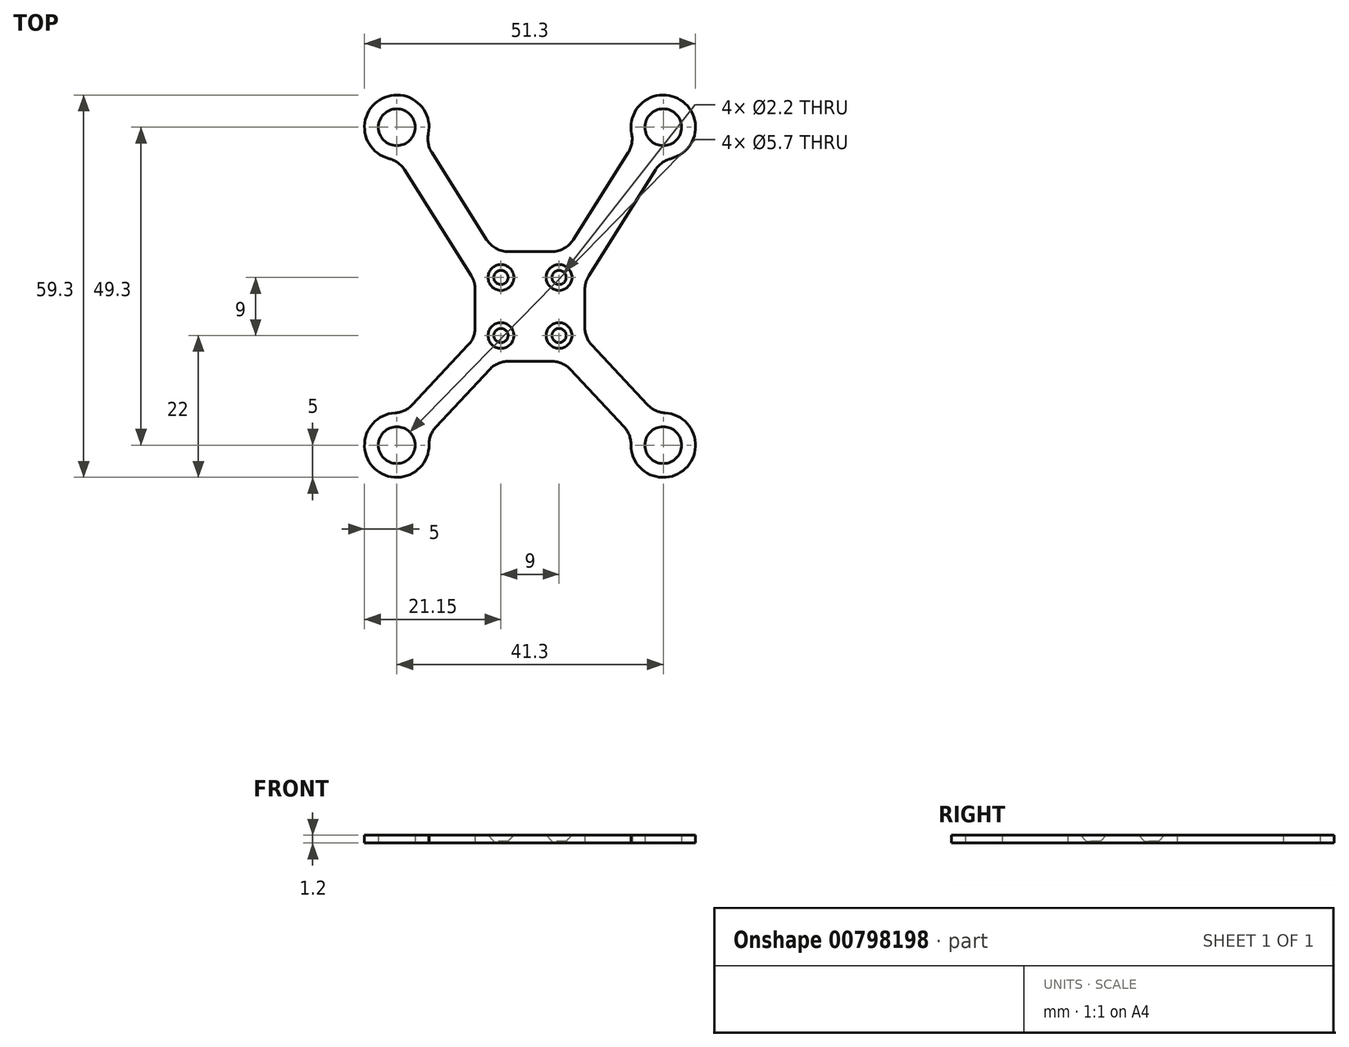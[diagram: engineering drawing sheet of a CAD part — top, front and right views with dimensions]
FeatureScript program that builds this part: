
annotation { "Feature Type Name" : "Feature", "Feature Type Description" : "" }
export const myFeature = defineFeature(function(context is Context, id is Id, definition is map)
    precondition{}
    {
        {
            var Q0;
            Q0=qCreatedBy(makeId("Top.planeOp"),FACE);
            var sketch = newSketch(context, id + "F0", { "sketchPlane" : qUnion([Q0])});
            skLineSegment(sketch, "E0.bottom", {"start": v(14.65, 24.65) * mm, "end": v(-14.65, 24.65) * mm});
            skLineSegment(sketch, "E0.top", {"start": v(14.65, -24.65) * mm, "end": v(-14.65, -24.65) * mm});
            skLineSegment(sketch, "E0.left", {"start": v(14.65, 24.65) * mm, "end": v(14.65, -24.65) * mm});
            skLineSegment(sketch, "E0.right", {"start": v(-14.65, 24.65) * mm, "end": v(-14.65, -24.65) * mm});
            skPoint(sketch, "E0.middle", {"position": v(0, 0) * mm});
            skLineSegment(sketch, "E1.bottom", {"start": v(4.5, 1.35) * mm, "end": v(-4.5, 1.35) * mm});
            skLineSegment(sketch, "E1.top", {"start": v(4.5, -7.65) * mm, "end": v(-4.5, -7.65) * mm});
            skLineSegment(sketch, "E1.left", {"start": v(4.5, 1.35) * mm, "end": v(4.5, -7.65) * mm});
            skLineSegment(sketch, "E1.right", {"start": v(-4.5, 1.35) * mm, "end": v(-4.5, -7.65) * mm});
            skPoint(sketch, "E1.middle", {"position": v(0, -3.15) * mm});
            skSolve(sketch);
        }
        {
            var Q0;
            Q0=qCreatedBy(makeId("Top.planeOp"),FACE);
            var sketch = newSketch(context, id + "F1", { "sketchPlane" : qUnion([Q0])});
            skLineSegment(sketch, "E2.bottom", {"start": v(8.5, 5.35) * mm, "end": v(-8.5, 5.35) * mm, "construction": true});
            skLineSegment(sketch, "E2.top", {"start": v(8.5, -11.65) * mm, "end": v(-8.5, -11.65) * mm, "construction": true});
            skLineSegment(sketch, "E2.left", {"start": v(8.5, 5.35) * mm, "end": v(8.5, -11.65) * mm, "construction": true});
            skLineSegment(sketch, "E2.right", {"start": v(-8.5, 5.35) * mm, "end": v(-8.5, -11.65) * mm, "construction": true});
            skPoint(sketch, "E2.middle", {"position": v(0, -3.15) * mm});
            skCircle(sketch, "E3", {"center": v(-4.5, 1.35) * mm, "radius": 1.1 * mm});
            skCircle(sketch, "E4", {"center": v(4.5, 1.35) * mm, "radius": 1.1 * mm});
            skCircle(sketch, "E5", {"center": v(4.5, -7.65) * mm, "radius": 1.1 * mm});
            skCircle(sketch, "E6", {"center": v(-4.5, -7.65) * mm, "radius": 1.1 * mm});
            skCircle(sketch, "E7", {"center": v(-20.65, -24.65) * mm, "radius": 2.85 * mm});
            skCircle(sketch, "E8", {"center": v(-20.65, -24.65) * mm, "radius": 5 * mm, "construction": true});
            skCircle(sketch, "E9.MirrorC", {"center": v(20.65, -24.65) * mm, "radius": 2.85 * mm});
            skCircle(sketch, "E10.MirrorC", {"center": v(20.65, -24.65) * mm, "radius": 5 * mm, "construction": true});
            skCircle(sketch, "E11.MirrorC", {"center": v(20.65, 24.65) * mm, "radius": 2.85 * mm});
            skCircle(sketch, "E12.MirrorC", {"center": v(20.65, 24.65) * mm, "radius": 5 * mm, "construction": true});
            skCircle(sketch, "E13.MirrorC", {"center": v(-20.65, 24.65) * mm, "radius": 2.85 * mm});
            skCircle(sketch, "E14.MirrorC", {"center": v(-20.65, 24.65) * mm, "radius": 5 * mm, "construction": true});
            skLineSegment(sketch, "E15", {"start": v(-20.65, 24.65) * mm, "end": v(-8.5, 5.35) * mm, "construction": true});
            skLineSegment(sketch, "E16", {"start": v(8.5, 5.35) * mm, "end": v(20.65, 24.65) * mm, "construction": true});
            skLineSegment(sketch, "E17", {"start": v(8.5, -11.65) * mm, "end": v(20.65, -24.65) * mm, "construction": true});
            skLineSegment(sketch, "E18", {"start": v(-8.5, -11.65) * mm, "end": v(-20.65, -24.65) * mm, "construction": true});
            skLineSegment(sketch, "E19", {"start": v(-19.52, -19.78) * mm, "end": v(-8.5, -7.99) * mm});
            skLineSegment(sketch, "E20", {"start": v(-15.87, -23.2) * mm, "end": v(-5.08, -11.65) * mm});
            skLineSegment(sketch, "E21", {"start": v(-20.46, 19.65) * mm, "end": v(-8.5, 0.66) * mm});
            skLineSegment(sketch, "E22", {"start": v(-5.55, 5.35) * mm, "end": v(-16.23, 22.32) * mm});
            skLineSegment(sketch, "E23", {"start": v(-14.11, 9.57) * mm, "end": v(-9.88, 12.24) * mm, "construction": true});
            skLineSegment(sketch, "E24", {"start": v(-8.65, -15.47) * mm, "end": v(-12.3, -12.06) * mm, "construction": true});
            skPoint(sketch, "E25", {"position": v(-12, 10.9) * mm});
            skPoint(sketch, "E26", {"position": v(-10.48, -13.76) * mm});
            skLineSegment(sketch, "E27.MirrorCS", {"start": v(15.87, -23.2) * mm, "end": v(5.08, -11.65) * mm});
            skLineSegment(sketch, "E28.MirrorCS", {"start": v(19.52, -19.78) * mm, "end": v(8.5, -7.99) * mm});
            skLineSegment(sketch, "E29.MirrorCS", {"start": v(20.46, 19.65) * mm, "end": v(8.5, 0.66) * mm});
            skLineSegment(sketch, "E30.MirrorCS", {"start": v(5.55, 5.35) * mm, "end": v(16.23, 22.32) * mm});
            skLineSegment(sketch, "E31", {"start": v(-5.55, 5.35) * mm, "end": v(5.55, 5.35) * mm});
            skLineSegment(sketch, "E32", {"start": v(8.5, 0.66) * mm, "end": v(8.5, -7.99) * mm});
            skLineSegment(sketch, "E33", {"start": v(5.08, -11.65) * mm, "end": v(-5.08, -11.65) * mm});
            skLineSegment(sketch, "E34", {"start": v(-8.5, -7.99) * mm, "end": v(-8.5, 0.66) * mm});
            skArc(sketch, "E35", {"start": v(-15.87, -23.2) * mm, "mid": v(-24.06, -28.3) * mm, "end": v(-19.52, -19.78) * mm});
            skArc(sketch, "E36", {"start": v(19.52, -19.78) * mm, "mid": v(24.06, -28.3) * mm, "end": v(15.87, -23.2) * mm});
            skArc(sketch, "E37", {"start": v(20.46, 19.65) * mm, "mid": v(23.31, 28.88) * mm, "end": v(16.23, 22.32) * mm});
            skArc(sketch, "E38", {"start": v(-16.23, 22.32) * mm, "mid": v(-23.31, 28.88) * mm, "end": v(-20.46, 19.65) * mm});
            skSolve(sketch);
        }
        {
            var Q0;
            Q0 = qSketchRegion(id + "F1", true);
            extrude(context, id + "F2", {"entities" : qUnion([Q0]), "depth" : 1.2 * mm, "offsetDistance" : 25 * mm});
        }
        {
            var Q0;
            Q0=makeQuery(id+"F2.opExtrude","SWEPT_EDGE",EDGE,{"disambiguationData":[OSD([sQuery(id+"F1.wireOp",EDGE,"E22"),sQuery(id+"F1.wireOp",EDGE,"E31")])]});
            var Q1;
            Q1=makeQuery(id+"F2.opExtrude","SWEPT_EDGE",EDGE,{"disambiguationData":[OSD([sQuery(id+"F1.wireOp",EDGE,"E30.MirrorCS"),sQuery(id+"F1.wireOp",EDGE,"E31")])]});
            var Q2;
            Q2=makeQuery(id+"F2.opExtrude","SWEPT_EDGE",EDGE,{"disambiguationData":[OSD([sQuery(id+"F1.wireOp",EDGE,"E22"),sQuery(id+"F1.wireOp",EDGE,"E38")])]});
            var Q3;
            Q3=makeQuery(id+"F2.opExtrude","SWEPT_EDGE",EDGE,{"disambiguationData":[OSD([sQuery(id+"F1.wireOp",EDGE,"E21"),sQuery(id+"F1.wireOp",EDGE,"E38")])]});
            var Q4;
            Q4=makeQuery(id+"F2.opExtrude","SWEPT_EDGE",EDGE,{"disambiguationData":[OSD([sQuery(id+"F1.wireOp",EDGE,"E30.MirrorCS"),sQuery(id+"F1.wireOp",EDGE,"E37")])]});
            var Q5;
            Q5=makeQuery(id+"F2.opExtrude","SWEPT_EDGE",EDGE,{"disambiguationData":[OSD([sQuery(id+"F1.wireOp",EDGE,"E29.MirrorCS"),sQuery(id+"F1.wireOp",EDGE,"E37")])]});
            var Q6;
            Q6=makeQuery(id+"F2.opExtrude","SWEPT_EDGE",EDGE,{"disambiguationData":[OSD([sQuery(id+"F1.wireOp",EDGE,"E29.MirrorCS"),sQuery(id+"F1.wireOp",EDGE,"E32")])]});
            var Q7;
            Q7=makeQuery(id+"F2.opExtrude","SWEPT_EDGE",EDGE,{"disambiguationData":[OSD([sQuery(id+"F1.wireOp",EDGE,"E28.MirrorCS"),sQuery(id+"F1.wireOp",EDGE,"E32")])]});
            var Q8;
            Q8=makeQuery(id+"F2.opExtrude","SWEPT_EDGE",EDGE,{"disambiguationData":[OSD([sQuery(id+"F1.wireOp",EDGE,"E28.MirrorCS"),sQuery(id+"F1.wireOp",EDGE,"E36")])]});
            var Q9;
            Q9=makeQuery(id+"F2.opExtrude","SWEPT_EDGE",EDGE,{"disambiguationData":[OSD([sQuery(id+"F1.wireOp",EDGE,"E27.MirrorCS"),sQuery(id+"F1.wireOp",EDGE,"E36")])]});
            var Q10;
            Q10=makeQuery(id+"F2.opExtrude","SWEPT_EDGE",EDGE,{"disambiguationData":[OSD([sQuery(id+"F1.wireOp",EDGE,"E27.MirrorCS"),sQuery(id+"F1.wireOp",EDGE,"E33")])]});
            var Q11;
            Q11=makeQuery(id+"F2.opExtrude","SWEPT_EDGE",EDGE,{"disambiguationData":[OSD([sQuery(id+"F1.wireOp",EDGE,"E20"),sQuery(id+"F1.wireOp",EDGE,"E33")])]});
            var Q12;
            Q12=makeQuery(id+"F2.opExtrude","SWEPT_EDGE",EDGE,{"disambiguationData":[OSD([sQuery(id+"F1.wireOp",EDGE,"E20"),sQuery(id+"F1.wireOp",EDGE,"E35")])]});
            var Q13;
            Q13=makeQuery(id+"F2.opExtrude","SWEPT_EDGE",EDGE,{"disambiguationData":[OSD([sQuery(id+"F1.wireOp",EDGE,"E21"),sQuery(id+"F1.wireOp",EDGE,"E34")])]});
            var Q14;
            Q14=makeQuery(id+"F2.opExtrude","SWEPT_EDGE",EDGE,{"disambiguationData":[OSD([sQuery(id+"F1.wireOp",EDGE,"E19"),sQuery(id+"F1.wireOp",EDGE,"E34")])]});
            var Q15;
            Q15=makeQuery(id+"F2.opExtrude","SWEPT_EDGE",EDGE,{"disambiguationData":[OSD([sQuery(id+"F1.wireOp",EDGE,"E19"),sQuery(id+"F1.wireOp",EDGE,"E35")])]});
            fillet(context, id + "F3", {"entities" : qUnion([Q0, Q1, Q2, Q3, Q4, Q5, Q6, Q7, Q8, Q9, Q10, Q11, Q12, Q13, Q14, Q15]), "radius" : 4 * mm, "tangentPropagation" : true, "allowEdgeOverflow" : false});
        }
        {
            var Q0;
            Q0=makeQuery(id+"F2.opExtrude","CAP_EDGE",EDGE,{"disambiguationData":[OSD([sQuery(id+"F1.wireOp",EDGE,"E3")])],"isStart":false});
            var Q1;
            Q1=makeQuery(id+"F2.opExtrude","CAP_EDGE",EDGE,{"disambiguationData":[OSD([sQuery(id+"F1.wireOp",EDGE,"E4")])],"isStart":false});
            var Q2;
            Q2=makeQuery(id+"F2.opExtrude","CAP_EDGE",EDGE,{"disambiguationData":[OSD([sQuery(id+"F1.wireOp",EDGE,"E5")])],"isStart":false});
            var Q3;
            Q3=makeQuery(id+"F2.opExtrude","CAP_EDGE",EDGE,{"disambiguationData":[OSD([sQuery(id+"F1.wireOp",EDGE,"E6")])],"isStart":false});
            chamfer(context, id + "F4", {"entities" : qUnion([Q0, Q1, Q2, Q3]), "width" : .9 * mm, "tangentPropagation" : true});
        }
    });
